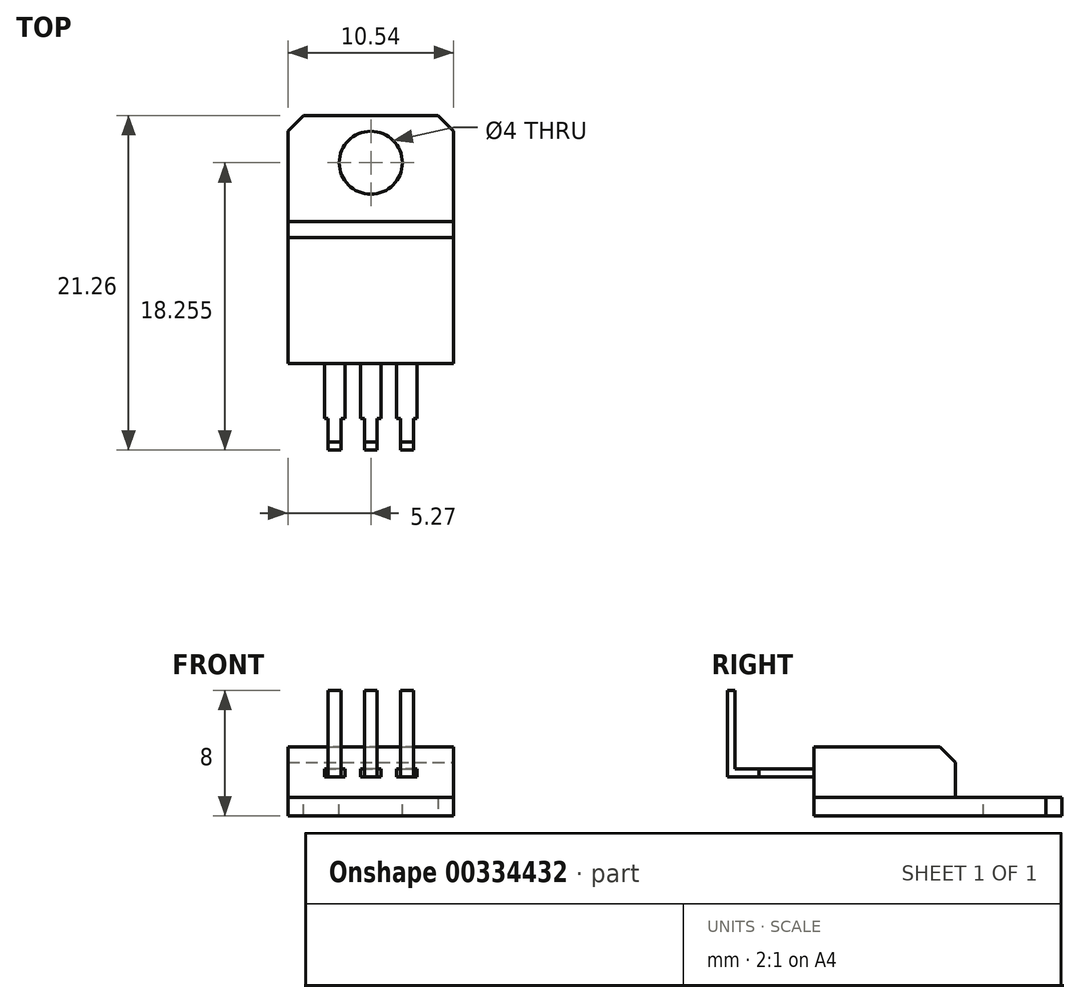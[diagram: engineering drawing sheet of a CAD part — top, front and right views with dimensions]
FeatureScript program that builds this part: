
annotation { "Feature Type Name" : "Feature", "Feature Type Description" : "" }
export const myFeature = defineFeature(function(context is Context, id is Id, definition is map)
    precondition{}
    {
        {
            var Q0;
            Q0=qCreatedBy(makeId("Top.planeOp"),FACE);
            var sketch = newSketch(context, id + "F0", { "sketchPlane" : qUnion([Q0])});
            skLineSegment(sketch, "E0.bottom", {"start": v(-5.26, 7.88) * mm, "end": v(5.27, 7.88) * mm});
            skLineSegment(sketch, "E0.top", {"start": v(-5.27, -7.88) * mm, "end": v(5.26, -7.88) * mm});
            skLineSegment(sketch, "E0.left", {"start": v(-5.26, 7.88) * mm, "end": v(-5.27, -7.88) * mm});
            skLineSegment(sketch, "E0.right", {"start": v(5.27, 7.88) * mm, "end": v(5.26, -7.88) * mm});
            skPoint(sketch, "E0.middle", {"position": v(0, 0) * mm});
            skSolve(sketch);
        }
        {
            var Q0;
            Q0=makeQuery(id+"F0.imprint","IMPRINT",FACE,{"disambiguationData":[TD([[makeQuery(id+"F0.imprint","IMPRINT",EDGE,{"derivedFrom":sQuery(id+"F0.wireOp",EDGE,"E0.bottom")}),-1.0]])]});
            extrude(context, id + "F1", {"entities" : qUnion([Q0]), "depth" : 1.2 * mm});
        }
        {
            var Q0;
            Q0=makeQuery(id+"F1.opExtrude","CAP_FACE",FACE,{"disambiguationData":[OSD([sQuery(id+"F0.wireOp",EDGE,"E0.bottom"),sQuery(id+"F0.wireOp",EDGE,"E0.top"),sQuery(id+"F0.wireOp",EDGE,"E0.left"),sQuery(id+"F0.wireOp",EDGE,"E0.right")])],"isStart":false});
            var sketch = newSketch(context, id + "F2", { "sketchPlane" : qUnion([Q0])});
            skLineSegment(sketch, "E1.bottom", {"start": v(-5.27, -7.88) * mm, "end": v(5.27, -7.88) * mm});
            skLineSegment(sketch, "E1.top", {"start": v(-5.27, 1.13) * mm, "end": v(5.27, 1.13) * mm});
            skLineSegment(sketch, "E1.left", {"start": v(-5.27, -7.88) * mm, "end": v(-5.27, 1.13) * mm});
            skLineSegment(sketch, "E1.right", {"start": v(5.27, -7.88) * mm, "end": v(5.27, 1.13) * mm});
            skSolve(sketch);
        }
        {
            var Q0;
            Q0=makeQuery(id+"F2.imprint","IMPRINT",FACE,{"disambiguationData":[TD([[makeQuery(id+"F2.imprint","IMPRINT",EDGE,{"derivedFrom":sQuery(id+"F2.wireOp",EDGE,"E1.bottom")}),1.0]])]});
            extrude(context, id + "F3", {"entities" : qUnion([Q0]), "depth" : (4.4 - 1.2) * mm});
        }
        {
            var Q0;
            Q0=makeQuery(id+"F3.opExtrude","CAP_EDGE",EDGE,{"disambiguationData":[OSD([sQuery(id+"F2.wireOp",EDGE,"E1.top")])],"isStart":false});
            var Q1;
            Q1=makeQuery(id+"F1.opExtrude","SWEPT_EDGE",EDGE,{"disambiguationData":[OSD([sQuery(id+"F0.wireOp",EDGE,"E0.bottom"),sQuery(id+"F0.wireOp",EDGE,"E0.right")])]});
            var Q2;
            Q2=makeQuery(id+"F1.opExtrude","SWEPT_EDGE",EDGE,{"disambiguationData":[OSD([sQuery(id+"F0.wireOp",EDGE,"E0.bottom"),sQuery(id+"F0.wireOp",EDGE,"E0.left")])]});
            chamfer(context, id + "F4", {"entities" : qUnion([Q0, Q1, Q2]), "width" : 1 * mm, "tangentPropagation" : true});
        }
        {
            var Q0;
            Q0=makeQuery(id+"F3.opExtrude","SWEPT_FACE",FACE,{"disambiguationData":[OSD([sQuery(id+"F2.wireOp",EDGE,"E1.bottom")])]});
            var sketch = newSketch(context, id + "F5", { "sketchPlane" : qUnion([Q0])});
            skLineSegment(sketch, "E2.bottom", {"start": v(-0.65, 3) * mm, "end": v(0.65, 3) * mm});
            skLineSegment(sketch, "E2.top", {"start": v(-0.65, 2.5) * mm, "end": v(0.65, 2.5) * mm});
            skLineSegment(sketch, "E2.left", {"start": v(-0.65, 3) * mm, "end": v(-0.65, 2.5) * mm});
            skLineSegment(sketch, "E2.right", {"start": v(0.65, 3) * mm, "end": v(0.65, 2.5) * mm});
            skLineSegment(sketch, "E3.bottom", {"start": v(-2.95, 3) * mm, "end": v(-1.65, 3) * mm});
            skLineSegment(sketch, "E3.top", {"start": v(-2.95, 2.5) * mm, "end": v(-1.65, 2.5) * mm});
            skLineSegment(sketch, "E3.left", {"start": v(-2.95, 3) * mm, "end": v(-2.95, 2.5) * mm});
            skLineSegment(sketch, "E3.right", {"start": v(-1.65, 3) * mm, "end": v(-1.65, 2.5) * mm});
            skLineSegment(sketch, "E4.bottom", {"start": v(2.95, 2.5) * mm, "end": v(1.65, 2.5) * mm});
            skLineSegment(sketch, "E4.top", {"start": v(2.95, 3) * mm, "end": v(1.65, 3) * mm});
            skLineSegment(sketch, "E4.left", {"start": v(2.95, 2.5) * mm, "end": v(2.95, 3) * mm});
            skLineSegment(sketch, "E4.right", {"start": v(1.65, 2.5) * mm, "end": v(1.65, 3) * mm});
            skPoint(sketch, "E5", {"position": v(0, 3) * mm});
            skSolve(sketch);
        }
        {
            var Q0;
            Q0=makeQuery(id+"F5.imprint","IMPRINT",FACE,{"disambiguationData":[TD([[makeQuery(id+"F5.imprint","IMPRINT",EDGE,{"derivedFrom":sQuery(id+"F5.wireOp",EDGE,"E3.bottom")}),-1.0]])]});
            var Q1;
            Q1=makeQuery(id+"F5.imprint","IMPRINT",FACE,{"disambiguationData":[TD([[makeQuery(id+"F5.imprint","IMPRINT",EDGE,{"derivedFrom":sQuery(id+"F5.wireOp",EDGE,"E2.bottom")}),-1.0]])]});
            var Q2;
            Q2=makeQuery(id+"F5.imprint","IMPRINT",FACE,{"disambiguationData":[TD([[makeQuery(id+"F5.imprint","IMPRINT",EDGE,{"derivedFrom":sQuery(id+"F5.wireOp",EDGE,"E4.bottom")}),-1.0]])]});
            extrude(context, id + "F6", {"entities" : qUnion([Q0, Q1, Q2]), "depth" : 3.5 * mm});
        }
        {
            var Q0;
            Q0=makeQuery(id+"F6.opExtrude","CAP_FACE",FACE,{"disambiguationData":[OSD([sQuery(id+"F5.wireOp",EDGE,"E3.bottom"),sQuery(id+"F5.wireOp",EDGE,"E3.top"),sQuery(id+"F5.wireOp",EDGE,"E3.left"),sQuery(id+"F5.wireOp",EDGE,"E3.right")])],"isStart":false});
            var sketch = newSketch(context, id + "F7", { "sketchPlane" : qUnion([Q0])});
            skLineSegment(sketch, "E6.bottom", {"start": v(-2.7, 3) * mm, "end": v(-1.9, 3) * mm});
            skLineSegment(sketch, "E6.top", {"start": v(-2.7, 2.5) * mm, "end": v(-1.9, 2.5) * mm});
            skLineSegment(sketch, "E6.left", {"start": v(-2.7, 3) * mm, "end": v(-2.7, 2.5) * mm});
            skLineSegment(sketch, "E6.right", {"start": v(-1.9, 3) * mm, "end": v(-1.9, 2.5) * mm});
            skLineSegment(sketch, "E7.bottom", {"start": v(-0.4, 3) * mm, "end": v(0.4, 3) * mm});
            skLineSegment(sketch, "E7.top", {"start": v(-0.4, 2.5) * mm, "end": v(0.4, 2.5) * mm});
            skLineSegment(sketch, "E7.left", {"start": v(-0.4, 3) * mm, "end": v(-0.4, 2.5) * mm});
            skLineSegment(sketch, "E7.right", {"start": v(0.4, 3) * mm, "end": v(0.4, 2.5) * mm});
            skLineSegment(sketch, "E8.bottom", {"start": v(1.9, 3) * mm, "end": v(2.7, 3) * mm});
            skLineSegment(sketch, "E8.top", {"start": v(1.9, 2.5) * mm, "end": v(2.7, 2.5) * mm});
            skLineSegment(sketch, "E8.left", {"start": v(1.9, 3) * mm, "end": v(1.9, 2.5) * mm});
            skLineSegment(sketch, "E8.right", {"start": v(2.7, 3) * mm, "end": v(2.7, 2.5) * mm});
            skPoint(sketch, "E9", {"position": v(2.3, 2.5) * mm});
            skPoint(sketch, "E10", {"position": v(2.3, 3) * mm});
            skPoint(sketch, "E11", {"position": v(0, 3) * mm});
            skPoint(sketch, "E12", {"position": v(0, 2.5) * mm});
            skPoint(sketch, "E13", {"position": v(-2.3, 3) * mm});
            skSolve(sketch);
        }
        {
            var Q0;
            Q0=makeQuery(id+"F7.imprint","IMPRINT",FACE,{"disambiguationData":[TD([[makeQuery(id+"F7.imprint","IMPRINT",EDGE,{"derivedFrom":sQuery(id+"F7.wireOp",EDGE,"E6.bottom")}),-1.0]])]});
            var Q1;
            Q1=makeQuery(id+"F7.imprint","IMPRINT",FACE,{"disambiguationData":[TD([[makeQuery(id+"F7.imprint","IMPRINT",EDGE,{"derivedFrom":sQuery(id+"F7.wireOp",EDGE,"E7.bottom")}),-1.0]])]});
            var Q2;
            Q2=makeQuery(id+"F7.imprint","IMPRINT",FACE,{"disambiguationData":[TD([[makeQuery(id+"F7.imprint","IMPRINT",EDGE,{"derivedFrom":sQuery(id+"F7.wireOp",EDGE,"E8.bottom")}),-1.0]])]});
            extrude(context, id + "F8", {"entities" : qUnion([Q0, Q1, Q2]), "operationType" : NewBodyOperationType.ADD, "depth" : 2 * mm});
        }
        {
            var Q0;
            Q0=makeQuery(id+"F8.boolean.opBoolean","MERGE",FACE,{"derivedFrom":[makeQuery(id+"F6.opExtrude","SWEPT_FACE",FACE,{"disambiguationData":[OSD([sQuery(id+"F5.wireOp",EDGE,"E3.top")])]}),makeQuery(id+"F8.opExtrude","SWEPT_FACE",FACE,{"disambiguationData":[OSD([sQuery(id+"F7.wireOp",EDGE,"E6.top")])]})]});
            var sketch = newSketch(context, id + "F9", { "sketchPlane" : qUnion([Q0])});
            skLineSegment(sketch, "E14.bottom", {"start": v(-2.7, 13.38) * mm, "end": v(-1.9, 13.38) * mm});
            skLineSegment(sketch, "E14.top", {"start": v(-2.7, 12.88) * mm, "end": v(-1.9, 12.88) * mm});
            skLineSegment(sketch, "E14.left", {"start": v(-2.7, 13.38) * mm, "end": v(-2.7, 12.88) * mm});
            skLineSegment(sketch, "E14.right", {"start": v(-1.9, 13.38) * mm, "end": v(-1.9, 12.88) * mm});
            skLineSegment(sketch, "E15.bottom", {"start": v(-0.4, 13.38) * mm, "end": v(0.4, 13.38) * mm});
            skLineSegment(sketch, "E15.top", {"start": v(-0.4, 12.88) * mm, "end": v(0.4, 12.88) * mm});
            skLineSegment(sketch, "E15.left", {"start": v(-0.4, 13.38) * mm, "end": v(-0.4, 12.88) * mm});
            skLineSegment(sketch, "E15.right", {"start": v(0.4, 13.38) * mm, "end": v(0.4, 12.88) * mm});
            skLineSegment(sketch, "E16.bottom", {"start": v(1.9, 13.38) * mm, "end": v(2.7, 13.38) * mm});
            skLineSegment(sketch, "E16.top", {"start": v(1.9, 12.88) * mm, "end": v(2.7, 12.88) * mm});
            skLineSegment(sketch, "E16.left", {"start": v(1.9, 13.38) * mm, "end": v(1.9, 12.88) * mm});
            skLineSegment(sketch, "E16.right", {"start": v(2.7, 13.38) * mm, "end": v(2.7, 12.88) * mm});
            skSolve(sketch);
        }
        {
            var Q0;
            Q0=makeQuery(id+"F9.imprint","IMPRINT",FACE,{"disambiguationData":[TD([[makeQuery(id+"F9.imprint","IMPRINT",EDGE,{"derivedFrom":sQuery(id+"F9.wireOp",EDGE,"E14.bottom")}),-1.0]])]});
            var Q1;
            Q1=makeQuery(id+"F9.imprint","IMPRINT",FACE,{"disambiguationData":[TD([[makeQuery(id+"F9.imprint","IMPRINT",EDGE,{"derivedFrom":sQuery(id+"F9.wireOp",EDGE,"E15.bottom")}),-1.0]])]});
            var Q2;
            Q2=makeQuery(id+"F9.imprint","IMPRINT",FACE,{"disambiguationData":[TD([[makeQuery(id+"F9.imprint","IMPRINT",EDGE,{"derivedFrom":sQuery(id+"F9.wireOp",EDGE,"E16.bottom")}),-1.0]])]});
            extrude(context, id + "F10", {"entities" : qUnion([Q0, Q1, Q2]), "operationType" : NewBodyOperationType.ADD, "oppositeDirection" : true, "depth" : (5 + 0.5) * mm});
        }
        {
            var Q0;
            Q0=makeQuery(id+"F1.opExtrude","CAP_FACE",FACE,{"disambiguationData":[OSD([sQuery(id+"F0.wireOp",EDGE,"E0.bottom"),sQuery(id+"F0.wireOp",EDGE,"E0.top"),sQuery(id+"F0.wireOp",EDGE,"E0.left"),sQuery(id+"F0.wireOp",EDGE,"E0.right")])],"isStart":false});
            var sketch = newSketch(context, id + "F11", { "sketchPlane" : qUnion([Q0])});
            skPoint(sketch, "E17", {"position": v(0, 4.88) * mm});
            skSolve(sketch);
        }
        {
            var Q0;
            Q0=sQuery(id+"F11.wireOp",VERTEX,"E17");
            var Q1;
            Q1=makeQuery(id+"F1.opExtrude","SWEPT_BODY",BODY,{"disambiguationData":[OSD([sQuery(id+"F0.wireOp",EDGE,"E0.bottom"),sQuery(id+"F0.wireOp",EDGE,"E0.top"),sQuery(id+"F0.wireOp",EDGE,"E0.left"),sQuery(id+"F0.wireOp",EDGE,"E0.right")])]});
            hole(context, id + "F12", {"style" : HoleStyle.SIMPLE, "endStyle" : HoleEndStyle.THROUGH, "holeDiameter" : 4 * mm, "tappedDepth" : 13.2 * mm, "tapClearance" : 3, "startFromSketch" : true, "locations" : qUnion([Q0]), "scope" : qUnion([Q1])});
        }
    });
